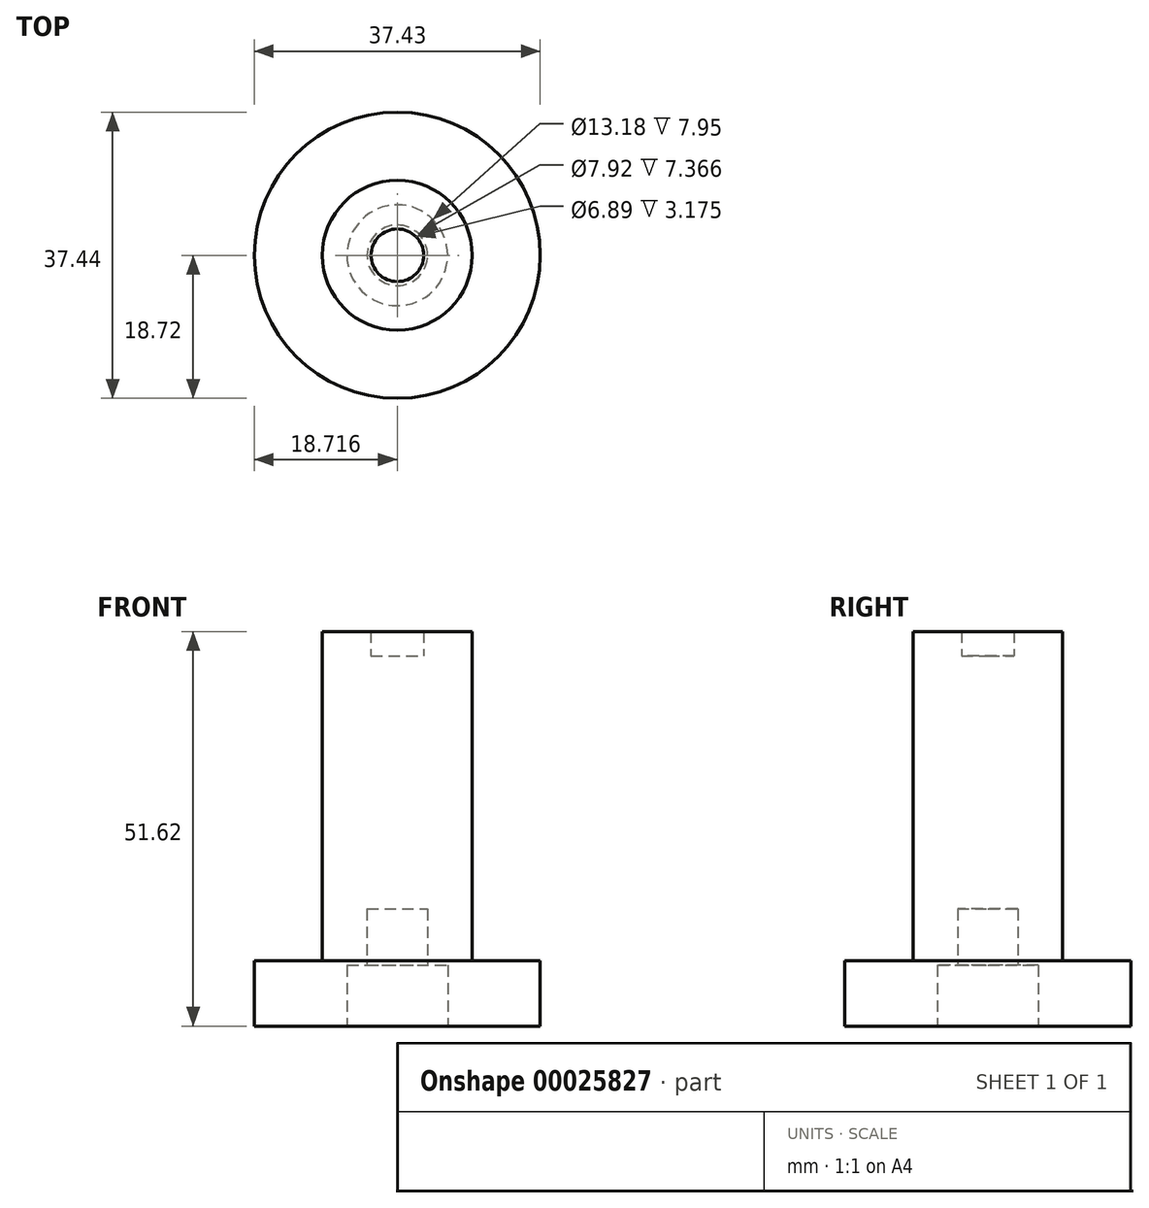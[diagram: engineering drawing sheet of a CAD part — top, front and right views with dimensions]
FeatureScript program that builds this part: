
annotation { "Feature Type Name" : "Feature", "Feature Type Description" : "" }
export const myFeature = defineFeature(function(context is Context, id is Id, definition is map)
    precondition{}
    {
        {
            var Q0;
            Q0=qCreatedBy(makeId("Front.planeOp"),FACE);
            var sketch = newSketch(context, id + "F0", { "sketchPlane" : qUnion([Q0])});
            skLineSegment(sketch, "E0", {"start": v(-47.18, 25.8) * mm, "end": v(-47.18, -17.28) * mm});
            skLineSegment(sketch, "E1", {"start": v(-47.18, -17.28) * mm, "end": v(-56.09, -17.28) * mm});
            skLineSegment(sketch, "E2", {"start": v(-56.09, -17.28) * mm, "end": v(-56.09, -25.8) * mm});
            skLineSegment(sketch, "E3", {"start": v(-56.09, -25.8) * mm, "end": v(-43.96, -25.8) * mm});
            skLineSegment(sketch, "E4", {"start": v(-43.96, -25.8) * mm, "end": v(-43.96, -17.86) * mm});
            skLineSegment(sketch, "E5", {"start": v(-43.96, -17.86) * mm, "end": v(-41.33, -17.86) * mm});
            skLineSegment(sketch, "E6", {"start": v(-41.33, -17.86) * mm, "end": v(-41.33, -10.5) * mm});
            skLineSegment(sketch, "E7", {"start": v(-41.33, -10.5) * mm, "end": v(-37.37, -10.5) * mm});
            skLineSegment(sketch, "E8", {"start": v(-37.37, -10.5) * mm, "end": v(-37.37, 22.63) * mm});
            skLineSegment(sketch, "E9", {"start": v(-37.37, 22.63) * mm, "end": v(-40.82, 22.63) * mm});
            skLineSegment(sketch, "E10", {"start": v(-40.82, 22.63) * mm, "end": v(-40.82, 25.8) * mm});
            skLineSegment(sketch, "E11", {"start": v(-40.82, 25.8) * mm, "end": v(-47.18, 25.8) * mm});
            skSolve(sketch);
        }
        {
            var Q0;
            Q0=makeQuery(id+"F0.imprint","IMPRINT",FACE,{"disambiguationData":[TD([[makeQuery(id+"F0.imprint","IMPRINT",EDGE,{"derivedFrom":sQuery(id+"F0.wireOp",EDGE,"E0")}),1.0]])]});
            var Q1;
            Q1=sQuery(id+"F0.wireOp",EDGE,"E8");
            revolve(context, id + "F1", {"entities" : qUnion([Q0]), "axis" : qUnion([Q1]), "revolveType" : RevolveType.FULL});
        }
    });
